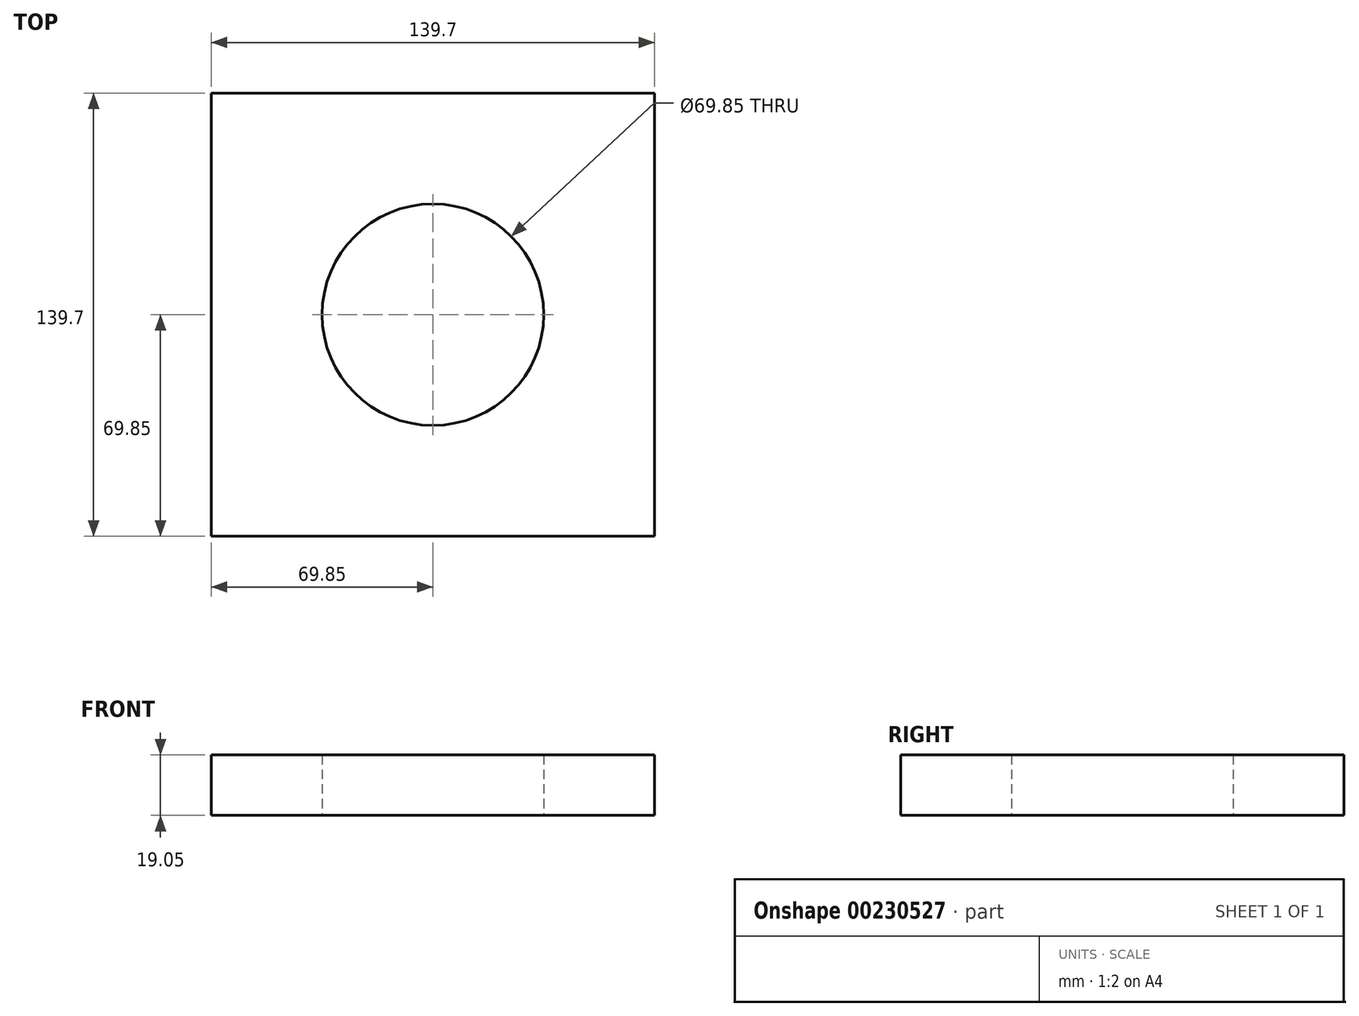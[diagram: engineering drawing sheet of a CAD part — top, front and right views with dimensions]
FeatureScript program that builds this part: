
annotation { "Feature Type Name" : "Feature", "Feature Type Description" : "" }
export const myFeature = defineFeature(function(context is Context, id is Id, definition is map)
    precondition{}
    {
        {
            var Q0;
            Q0=qCreatedBy(makeId("Top.planeOp"),FACE);
            var sketch = newSketch(context, id + "F0", { "sketchPlane" : qUnion([Q0])});
            skLineSegment(sketch, "E0.bottom", {"start": v(-69.85, -69.85) * mm, "end": v(69.85, -69.85) * mm});
            skLineSegment(sketch, "E0.top", {"start": v(-69.85, 69.85) * mm, "end": v(69.85, 69.85) * mm});
            skLineSegment(sketch, "E0.left", {"start": v(-69.85, -69.85) * mm, "end": v(-69.85, 69.85) * mm});
            skLineSegment(sketch, "E0.right", {"start": v(69.85, -69.85) * mm, "end": v(69.85, 69.85) * mm});
            skPoint(sketch, "E0.middle", {"position": v(0, 0) * mm});
            skCircle(sketch, "E1", {"center": v(0, 0) * mm, "radius": 34.93 * mm});
            skSolve(sketch);
        }
        {
            var Q0;
            Q0=makeQuery(id+"F0.imprint","IMPRINT",FACE,{"disambiguationData":[TD([[makeQuery(id+"F0.imprint","IMPRINT",EDGE,{"derivedFrom":sQuery(id+"F0.wireOp",EDGE,"E0.bottom")}),1.0]])]});
            extrude(context, id + "F1", {"entities" : qUnion([Q0]), "depth" : 19.05 * mm});
        }
    });
